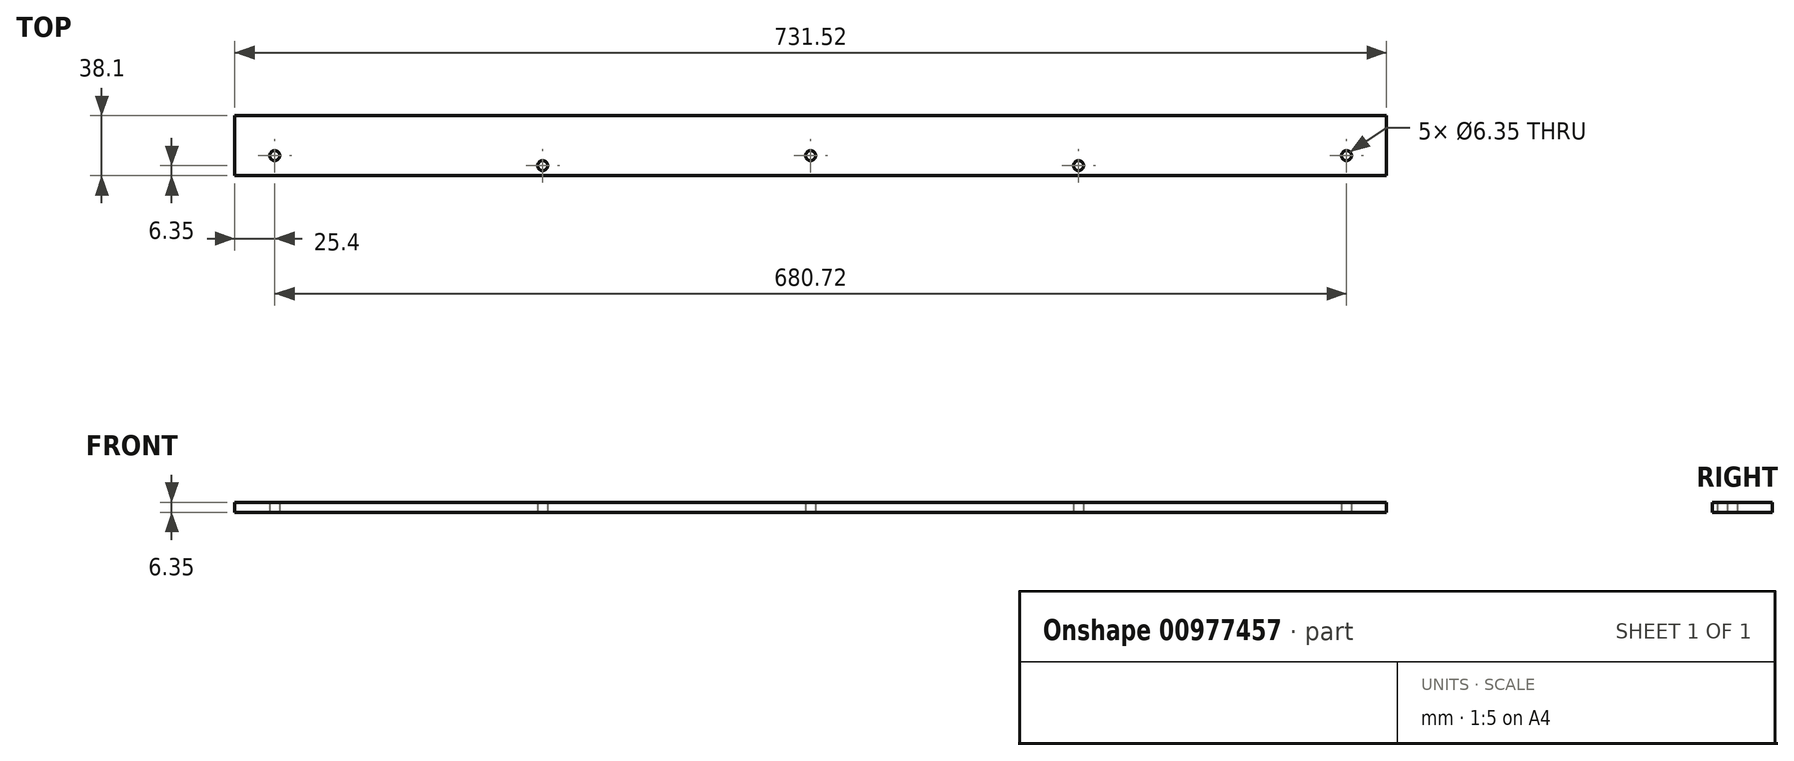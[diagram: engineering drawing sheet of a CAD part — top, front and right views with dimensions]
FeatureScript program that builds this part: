
annotation { "Feature Type Name" : "Feature", "Feature Type Description" : "" }
export const myFeature = defineFeature(function(context is Context, id is Id, definition is map)
    precondition{}
    {
        {
            var Q0;
            Q0=qCreatedBy(makeId("Top.planeOp"),FACE);
            var sketch = newSketch(context, id + "F0", { "sketchPlane" : qUnion([Q0])});
            skLineSegment(sketch, "E0.bottom", {"start": v(365.76, 19.05) * mm, "end": v(-365.76, 19.05) * mm});
            skLineSegment(sketch, "E0.top", {"start": v(365.76, -19.05) * mm, "end": v(-365.76, -19.05) * mm});
            skLineSegment(sketch, "E0.left", {"start": v(365.76, 19.05) * mm, "end": v(365.76, -19.05) * mm});
            skLineSegment(sketch, "E0.right", {"start": v(-365.76, 19.05) * mm, "end": v(-365.76, -19.05) * mm});
            skPoint(sketch, "E0.middle", {"position": v(0, 0) * mm});
            skCircle(sketch, "E1", {"center": v(0, -6.35) * mm, "radius": 3.18 * mm});
            skCircle(sketch, "E2", {"center": v(340.36, -6.35) * mm, "radius": 3.18 * mm});
            skCircle(sketch, "E3", {"center": v(170.18, -12.7) * mm, "radius": 3.18 * mm});
            skCircle(sketch, "E4.MirrorC", {"center": v(-170.18, -12.7) * mm, "radius": 3.18 * mm});
            skCircle(sketch, "E5.MirrorC", {"center": v(-340.36, -6.35) * mm, "radius": 3.18 * mm});
            skSolve(sketch);
        }
        {
            var Q0;
            Q0 = qSketchRegion(id + "F0", true);
            extrude(context, id + "F1", {"entities" : qUnion([Q0]), "depth" : 6.35 * mm, "offsetDistance" : 25.4 * mm});
        }
    });
